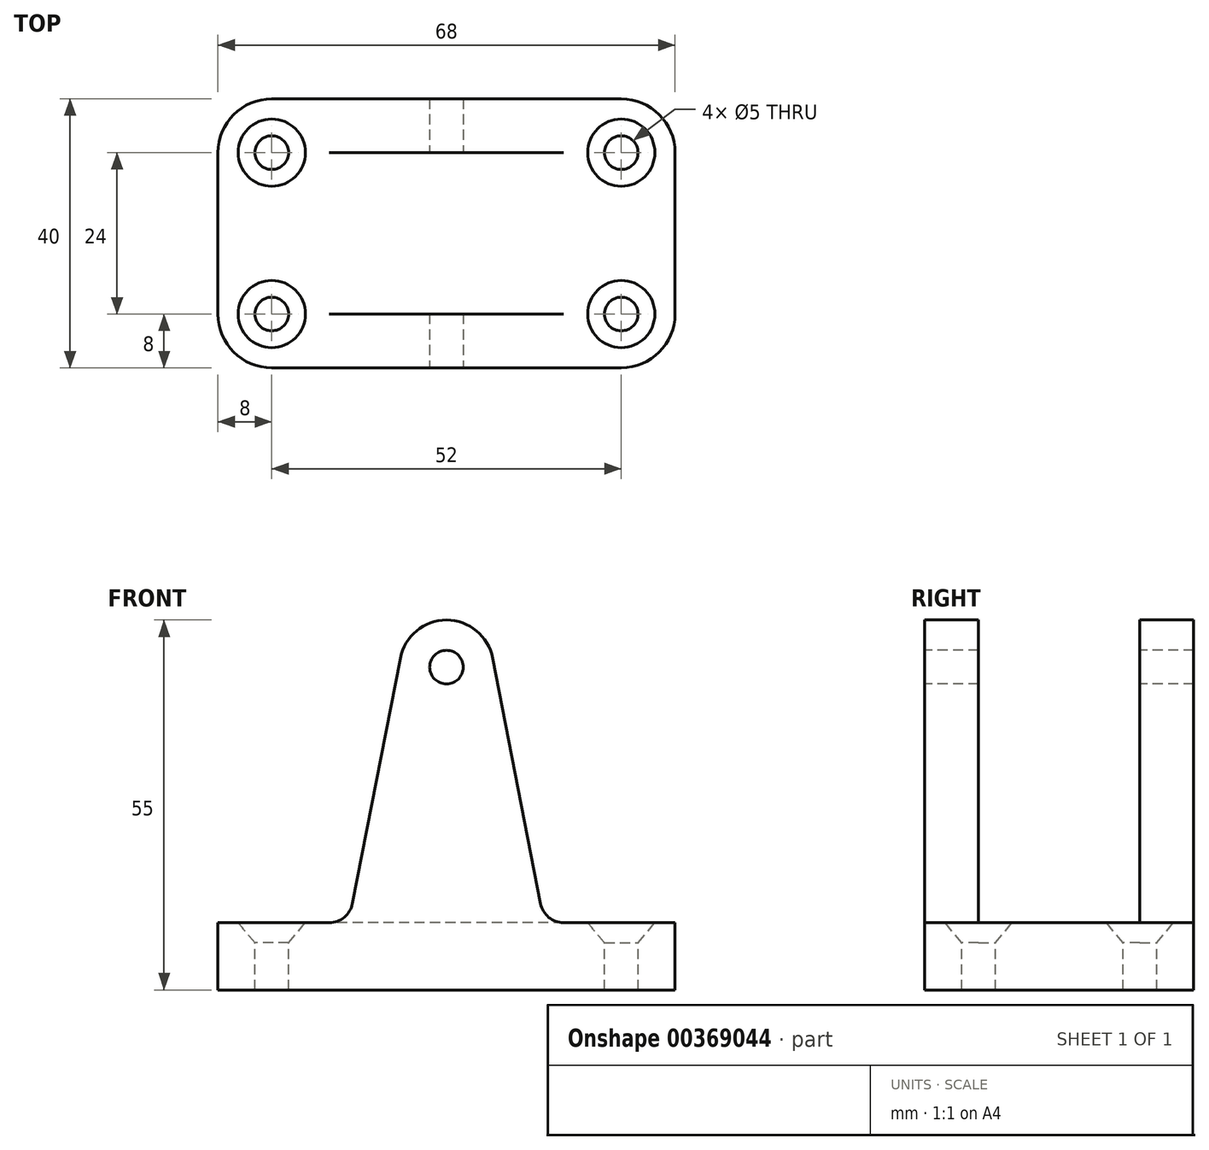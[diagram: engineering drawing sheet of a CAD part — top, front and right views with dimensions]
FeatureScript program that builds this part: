
annotation { "Feature Type Name" : "Feature", "Feature Type Description" : "" }
export const myFeature = defineFeature(function(context is Context, id is Id, definition is map)
    precondition{}
    {
        {
            var Q0;
            Q0=qCreatedBy(makeId("Top.planeOp"),FACE);
            var sketch = newSketch(context, id + "F0", { "sketchPlane" : qUnion([Q0])});
            skPoint(sketch, "E0.middle", {"position": v(0, 0) * mm});
            skLineSegment(sketch, "E1.bottom", {"start": v(26, 20) * mm, "end": v(-26, 20) * mm});
            skLineSegment(sketch, "E1.top", {"start": v(26, -20) * mm, "end": v(-26, -20) * mm});
            skLineSegment(sketch, "E1.left", {"start": v(34, 12) * mm, "end": v(34, -12) * mm});
            skLineSegment(sketch, "E1.right", {"start": v(-34, 12) * mm, "end": v(-34, -12) * mm});
            skPoint(sketch, "E2.visualSharp", {"position": v(-34, -20) * mm});
            skArc(sketch, "E2.filletArc", {"start": v(-34, -12) * mm, "mid": v(-31.66, -17.66) * mm, "end": v(-26, -20) * mm});
            skPoint(sketch, "E3.visualSharp", {"position": v(-34, 20) * mm});
            skArc(sketch, "E3.filletArc", {"start": v(-26, 20) * mm, "mid": v(-31.66, 17.66) * mm, "end": v(-34, 12) * mm});
            skPoint(sketch, "E4.visualSharp", {"position": v(34, 20) * mm});
            skArc(sketch, "E4.filletArc", {"start": v(34, 12) * mm, "mid": v(31.66, 17.66) * mm, "end": v(26, 20) * mm});
            skPoint(sketch, "E5.visualSharp", {"position": v(34, -20) * mm});
            skArc(sketch, "E5.filletArc", {"start": v(26, -20) * mm, "mid": v(31.66, -17.66) * mm, "end": v(34, -12) * mm});
            skSolve(sketch);
        }
        {
            var Q0;
            Q0 = qSketchRegion(id + "F0", true);
            extrude(context, id + "F1", {"entities" : qUnion([Q0]), "oppositeDirection" : true, "depth" : 10 * mm});
        }
        {
            var Q0;
            Q0=makeQuery(id+"F1.opExtrude","CAP_FACE",FACE,{"disambiguationData":[OSD([sQuery(id+"F0.wireOp",EDGE,"E1.bottom"),sQuery(id+"F0.wireOp",EDGE,"E1.top"),sQuery(id+"F0.wireOp",EDGE,"E1.left"),sQuery(id+"F0.wireOp",EDGE,"E1.right"),sQuery(id+"F0.wireOp",EDGE,"E2.filletArc"),sQuery(id+"F0.wireOp",EDGE,"E3.filletArc"),sQuery(id+"F0.wireOp",EDGE,"E4.filletArc"),sQuery(id+"F0.wireOp",EDGE,"E5.filletArc")])],"isStart":true});
            var sketch = newSketch(context, id + "F2", { "sketchPlane" : qUnion([Q0])});
            skCircle(sketch, "E6", {"center": v(-26, 12) * mm, "radius": 2.5 * mm});
            skCircle(sketch, "E7", {"center": v(26, 12) * mm, "radius": 2.5 * mm});
            skCircle(sketch, "E8", {"center": v(26, -12) * mm, "radius": 2.5 * mm});
            skCircle(sketch, "E9", {"center": v(-26, -12) * mm, "radius": 2.5 * mm});
            skSolve(sketch);
        }
        {
            var Q0;
            Q0=makeQuery(id+"F2.imprint","IMPRINT",FACE,{"disambiguationData":[TD([[makeQuery(id+"F2.imprint","IMPRINT",EDGE,{"derivedFrom":sQuery(id+"F2.wireOp",EDGE,"E6")}),1.0]])]});
            var Q1;
            Q1=makeQuery(id+"F2.imprint","IMPRINT",FACE,{"disambiguationData":[TD([[makeQuery(id+"F2.imprint","IMPRINT",EDGE,{"derivedFrom":sQuery(id+"F2.wireOp",EDGE,"E9")}),1.0]])]});
            var Q2;
            Q2=makeQuery(id+"F2.imprint","IMPRINT",FACE,{"disambiguationData":[TD([[makeQuery(id+"F2.imprint","IMPRINT",EDGE,{"derivedFrom":sQuery(id+"F2.wireOp",EDGE,"E8")}),1.0]])]});
            var Q3;
            Q3=makeQuery(id+"F2.imprint","IMPRINT",FACE,{"disambiguationData":[TD([[makeQuery(id+"F2.imprint","IMPRINT",EDGE,{"derivedFrom":sQuery(id+"F2.wireOp",EDGE,"E7")}),1.0]])]});
            extrude(context, id + "F3", {"entities" : qUnion([Q0, Q1, Q2, Q3]), "operationType" : NewBodyOperationType.REMOVE, "oppositeDirection" : true, "depth" : 25 * mm});
        }
        {
            var Q0;
            Q0=makeQuery(id+"F1.opExtrude","SWEPT_FACE",FACE,{"disambiguationData":[OSD([sQuery(id+"F0.wireOp",EDGE,"E1.top")])]});
            var sketch = newSketch(context, id + "F4", { "sketchPlane" : qUnion([Q0])});
            skCircle(sketch, "E10", {"center": v(0, 38) * mm, "radius": 2.5 * mm});
            skCircle(sketch, "E11", {"center": v(0, 38) * mm, "radius": 7 * mm});
            skLineSegment(sketch, "E12", {"start": v(-14, 2.83) * mm, "end": v(-6.87, 39.34) * mm});
            skArc(sketch, "E13.filletArc", {"start": v(-17.44, 0) * mm, "mid": v(-15.21, 0.8) * mm, "end": v(-14, 2.83) * mm});
            skLineSegment(sketch, "E14", {"start": v(0, 0) * mm, "end": v(-20.16, 0) * mm});
            skLineSegment(sketch, "E15.MirrorCS", {"start": v(14, 2.83) * mm, "end": v(6.87, 39.34) * mm});
            skArc(sketch, "E16.MirrorCS", {"start": v(17.44, 0) * mm, "mid": v(15.21, 0.8) * mm, "end": v(14, 2.83) * mm});
            skLineSegment(sketch, "E17.MirrorCS", {"start": v(0, 0) * mm, "end": v(20.16, 0) * mm});
            skSolve(sketch);
        }
        {
            var Q0;
            {var subQ4=sQuery(id+"F4.wireOp",EDGE,"E12");Q0=makeQuery(id+"F4.imprint","IMPRINT",FACE,{"disambiguationData":[TD([[makeQuery(id+"F4.imprint","IMPRINT",EDGE,{"derivedFrom":subQ4}),-1.0]])]});}
            var Q1;
            Q1=makeQuery(id+"F4.imprint","IMPRINT",FACE,{"disambiguationData":[TD([[makeQuery(id+"F4.imprint","IMPRINT",EDGE,{"derivedFrom":sQuery(id+"F4.wireOp",EDGE,"E10")}),-1.0]])]});
            extrude(context, id + "F5", {"entities" : qUnion([Q0, Q1]), "operationType" : NewBodyOperationType.ADD, "oppositeDirection" : true, "depth" : 8 * mm});
        }
        {
            var Q0;
            Q0 = qSketchRegion(id + "F4", true);
            extrude(context, id + "F6", {"entities" : qUnion([Q0]), "operationType" : NewBodyOperationType.ADD, "oppositeDirection" : true, "depth" : 40 * mm, "hasSecondDirection" : true, "secondDirectionOppositeDirection" : true, "secondDirectionDepth" : 32 * mm});
        }
        {
            var Q0;
            Q0=makeQuery(id+"F5.boolean.opBoolean","MERGE",FACE,{"derivedFrom":[makeQuery(id+"F1.opExtrude","SWEPT_FACE",FACE,{"disambiguationData":[OSD([sQuery(id+"F0.wireOp",EDGE,"E1.top")])]}),makeQuery(id+"F5.opExtrude","CAP_FACE",FACE,{"disambiguationData":[OSD([sQuery(id+"F4.wireOp",EDGE,"E10"),sQuery(id+"F4.wireOp",EDGE,"E11"),sQuery(id+"F4.wireOp",EDGE,"E12"),sQuery(id+"F4.wireOp",EDGE,"E13.filletArc"),sQuery(id+"F4.wireOp",EDGE,"E14"),sQuery(id+"F4.wireOp",EDGE,"E15.MirrorCS"),sQuery(id+"F4.wireOp",EDGE,"E16.MirrorCS"),sQuery(id+"F4.wireOp",EDGE,"E17.MirrorCS")])],"isStart":true})]});
            cPlane(context, id + "F7", {"entities" : qUnion([Q0]), "cplaneType" : CPlaneType.OFFSET, "offset" : 8 * mm, "oppositeDirection" : true, "width" : 150 * mm, "height" : 150 * mm});
        }
        {
            var Q0;
            Q0=qCreatedBy(id+"F7.planeOp",FACE);
            var sketch = newSketch(context, id + "F8", { "sketchPlane" : qUnion([Q0])});
            skLineSegment(sketch, "E18", {"start": v(-26, 0) * mm, "end": v(-26, -3) * mm});
            skLineSegment(sketch, "E19", {"start": v(-26, -3) * mm, "end": v(-23.5, -3) * mm});
            skLineSegment(sketch, "E20", {"start": v(-26, 0) * mm, "end": v(-21, 0) * mm});
            skLineSegment(sketch, "E21", {"start": v(-21, 0) * mm, "end": v(-23.5, -3) * mm});
            skSolve(sketch);
        }
        {
            var Q0;
            Q0 = qSketchRegion(id + "F8", true);
            var Q1;
            Q1=sQuery(id+"F8.wireOp",EDGE,"E18");
            revolve(context, id + "F9", {"operationType" : NewBodyOperationType.REMOVE, "entities" : qUnion([Q0]), "axis" : qUnion([Q1]), "revolveType" : RevolveType.FULL, "oppositeDirection" : true});
        }
        {
            var Q0;
            Q0=qCreatedBy(id+"F7.planeOp",FACE);
            var sketch = newSketch(context, id + "F10", { "sketchPlane" : qUnion([Q0])});
            skLineSegment(sketch, "E22", {"start": v(26, 0) * mm, "end": v(26, -3) * mm});
            skLineSegment(sketch, "E23", {"start": v(26, -3) * mm, "end": v(28.5, -3) * mm});
            skLineSegment(sketch, "E24", {"start": v(28.5, -3) * mm, "end": v(31, 0) * mm});
            skLineSegment(sketch, "E25", {"start": v(31, 0) * mm, "end": v(26, 0) * mm});
            skSolve(sketch);
        }
        {
            var Q0;
            Q0 = qSketchRegion(id + "F10", true);
            var Q1;
            Q1=sQuery(id+"F10.wireOp",EDGE,"E22");
            revolve(context, id + "F11", {"operationType" : NewBodyOperationType.REMOVE, "entities" : qUnion([Q0]), "axis" : qUnion([Q1]), "revolveType" : RevolveType.FULL, "oppositeDirection" : true});
        }
        {
            var Q0;
            Q0=makeQuery(id+"F6.boolean.opBoolean","MERGE",FACE,{"derivedFrom":[makeQuery(id+"F1.opExtrude","SWEPT_FACE",FACE,{"disambiguationData":[OSD([sQuery(id+"F0.wireOp",EDGE,"E1.bottom")])]}),makeQuery(id+"F6.opExtrude","CAP_FACE",FACE,{"disambiguationData":[OSD([sQuery(id+"F4.wireOp",EDGE,"E10"),sQuery(id+"F4.wireOp",EDGE,"E11"),sQuery(id+"F4.wireOp",EDGE,"E12"),sQuery(id+"F4.wireOp",EDGE,"E13.filletArc"),sQuery(id+"F4.wireOp",EDGE,"E14"),sQuery(id+"F4.wireOp",EDGE,"E15.MirrorCS"),sQuery(id+"F4.wireOp",EDGE,"E16.MirrorCS"),sQuery(id+"F4.wireOp",EDGE,"E17.MirrorCS")])],"isStart":false})]});
            cPlane(context, id + "F12", {"entities" : qUnion([Q0]), "cplaneType" : CPlaneType.OFFSET, "offset" : 8 * mm, "oppositeDirection" : true, "width" : 150 * mm, "height" : 150 * mm});
        }
        {
            var Q0;
            Q0=qCreatedBy(id+"F12.planeOp",FACE);
            var sketch = newSketch(context, id + "F13", { "sketchPlane" : qUnion([Q0])});
            skLineSegment(sketch, "E26", {"start": v(-26, 0) * mm, "end": v(-31, 0) * mm});
            skLineSegment(sketch, "E27", {"start": v(-26, 0) * mm, "end": v(-26, -3) * mm});
            skLineSegment(sketch, "E28", {"start": v(-26, -3) * mm, "end": v(-28.5, -3) * mm});
            skLineSegment(sketch, "E29", {"start": v(-28.5, -3) * mm, "end": v(-31, 0) * mm});
            skSolve(sketch);
        }
        {
            var Q0;
            Q0 = qSketchRegion(id + "F13", true);
            var Q1;
            Q1=sQuery(id+"F13.wireOp",EDGE,"E27");
            revolve(context, id + "F14", {"operationType" : NewBodyOperationType.REMOVE, "entities" : qUnion([Q0]), "axis" : qUnion([Q1]), "revolveType" : RevolveType.FULL, "oppositeDirection" : true});
        }
        {
            var Q0;
            Q0=qCreatedBy(id+"F12.planeOp",FACE);
            var sketch = newSketch(context, id + "F15", { "sketchPlane" : qUnion([Q0])});
            skLineSegment(sketch, "E30", {"start": v(26, 0) * mm, "end": v(26, -3) * mm});
            skLineSegment(sketch, "E31", {"start": v(26, -3) * mm, "end": v(28.5, -3) * mm});
            skLineSegment(sketch, "E32", {"start": v(28.5, -3) * mm, "end": v(31, 0) * mm});
            skLineSegment(sketch, "E33", {"start": v(31, 0) * mm, "end": v(26, 0) * mm});
            skSolve(sketch);
        }
        {
            var Q0;
            Q0 = qSketchRegion(id + "F15", true);
            var Q1;
            Q1=sQuery(id+"F15.wireOp",EDGE,"E30");
            revolve(context, id + "F16", {"operationType" : NewBodyOperationType.REMOVE, "entities" : qUnion([Q0]), "axis" : qUnion([Q1]), "revolveType" : RevolveType.FULL, "oppositeDirection" : true});
        }
    });
